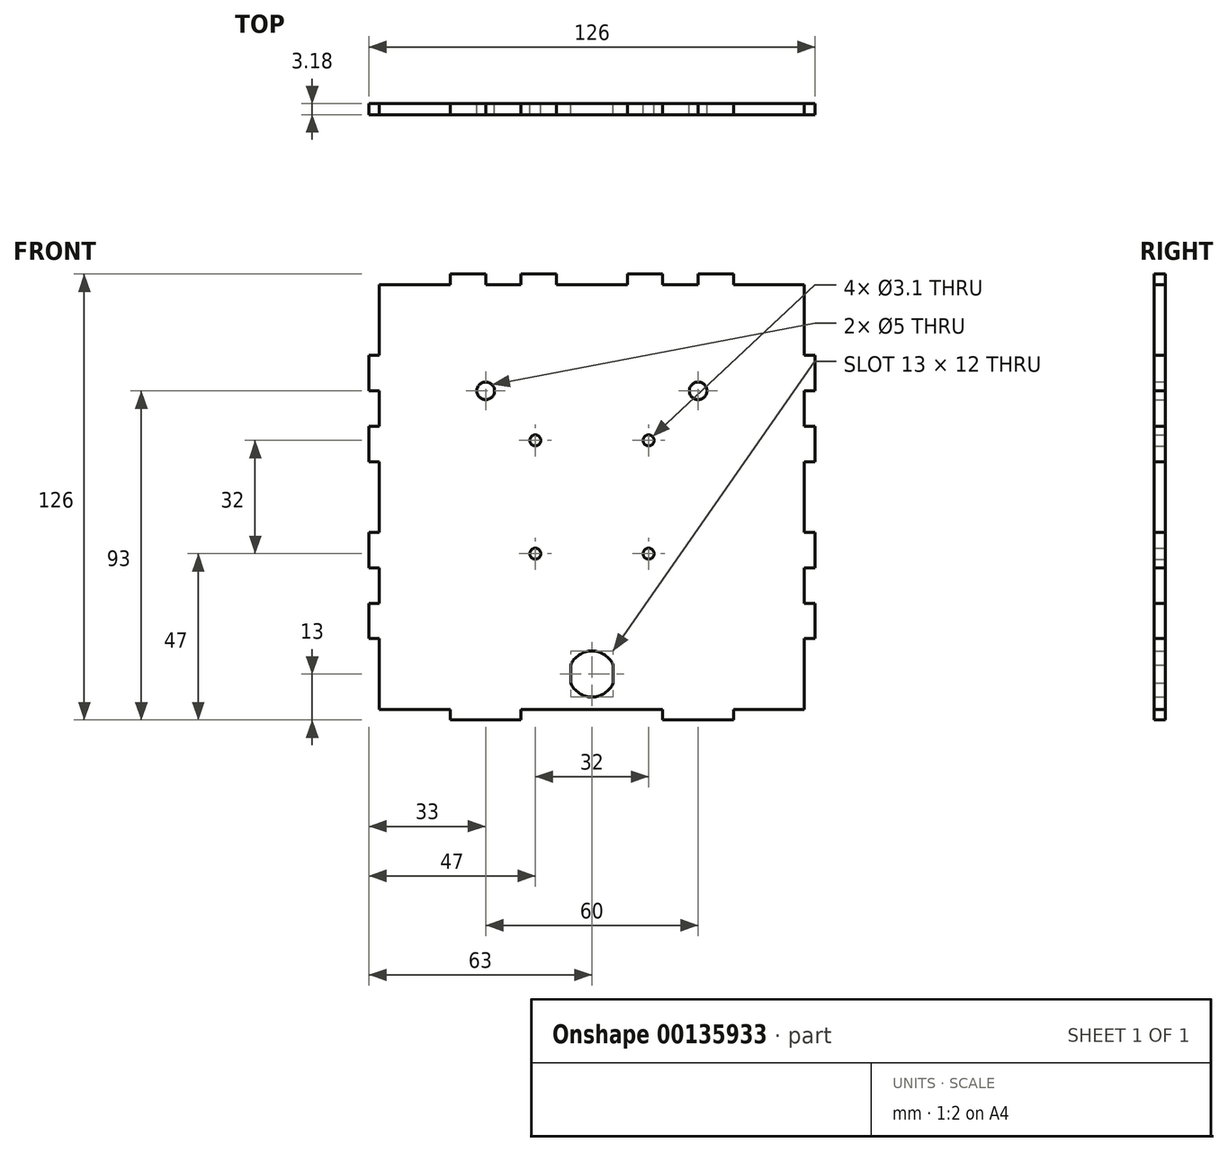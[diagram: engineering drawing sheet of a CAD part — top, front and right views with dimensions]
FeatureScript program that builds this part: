
annotation { "Feature Type Name" : "Feature", "Feature Type Description" : "" }
export const myFeature = defineFeature(function(context is Context, id is Id, definition is map)
    precondition{}
    {
        {
            var Q0;
            Q0=qCreatedBy(makeId("Front.planeOp"),FACE);
            var sketch = newSketch(context, id + "F0", { "sketchPlane" : qUnion([Q0])});
            skCircle(sketch, "E0", {"center": v(16, 16) * mm, "radius": 1.55 * mm});
            skCircle(sketch, "E1.1.0", {"center": v(-16, 16) * mm, "radius": 1.55 * mm});
            skCircle(sketch, "E1.2.0", {"center": v(-16, -16) * mm, "radius": 1.55 * mm});
            skCircle(sketch, "E1.3.0", {"center": v(16, -16) * mm, "radius": 1.55 * mm});
            skPoint(sketch, "E1.center", {"position": v(0, 0) * mm});
            skLineSegment(sketch, "E2", {"start": v(0, 60) * mm, "end": v(10, 60) * mm});
            skLineSegment(sketch, "E3", {"start": v(10, 60) * mm, "end": v(10, 63) * mm});
            skLineSegment(sketch, "E4", {"start": v(10, 63) * mm, "end": v(20, 63) * mm});
            skLineSegment(sketch, "E5", {"start": v(20, 63) * mm, "end": v(20, 60) * mm});
            skLineSegment(sketch, "E6", {"start": v(20, 60) * mm, "end": v(30, 60) * mm});
            skLineSegment(sketch, "E7", {"start": v(30, 60) * mm, "end": v(30, 63) * mm});
            skLineSegment(sketch, "E8", {"start": v(30, 63) * mm, "end": v(40, 63) * mm});
            skLineSegment(sketch, "E9", {"start": v(40, 63) * mm, "end": v(40, 60) * mm});
            skLineSegment(sketch, "E10", {"start": v(40, 60) * mm, "end": v(60, 60) * mm});
            skLineSegment(sketch, "E11", {"start": v(60, 60) * mm, "end": v(60, 40) * mm});
            skLineSegment(sketch, "E12", {"start": v(60, 40) * mm, "end": v(63, 40) * mm});
            skLineSegment(sketch, "E13", {"start": v(63, 40) * mm, "end": v(63, 30) * mm});
            skLineSegment(sketch, "E14", {"start": v(63, 30) * mm, "end": v(60, 30) * mm});
            skLineSegment(sketch, "E15", {"start": v(60, 30) * mm, "end": v(60, 20) * mm});
            skLineSegment(sketch, "E16", {"start": v(60, 20) * mm, "end": v(63, 20) * mm});
            skLineSegment(sketch, "E17", {"start": v(63, 20) * mm, "end": v(63, 10) * mm});
            skLineSegment(sketch, "E18", {"start": v(63, 10) * mm, "end": v(60, 10) * mm});
            skLineSegment(sketch, "E19", {"start": v(60, 10) * mm, "end": v(60, -10) * mm});
            skLineSegment(sketch, "E20", {"start": v(60, -10) * mm, "end": v(63, -10) * mm});
            skLineSegment(sketch, "E21", {"start": v(63, -10) * mm, "end": v(63, -20) * mm});
            skLineSegment(sketch, "E22", {"start": v(63, -20) * mm, "end": v(60, -20) * mm});
            skLineSegment(sketch, "E23", {"start": v(60, -20) * mm, "end": v(60, -30) * mm});
            skLineSegment(sketch, "E24", {"start": v(60, -30) * mm, "end": v(63, -30) * mm});
            skLineSegment(sketch, "E25", {"start": v(63, -30) * mm, "end": v(63, -40) * mm});
            skLineSegment(sketch, "E26", {"start": v(63, -40) * mm, "end": v(60, -40) * mm});
            skLineSegment(sketch, "E27", {"start": v(60, -40) * mm, "end": v(60, -60) * mm});
            skLineSegment(sketch, "E28", {"start": v(60, -60) * mm, "end": v(40, -60) * mm});
            skLineSegment(sketch, "E29", {"start": v(40, -60) * mm, "end": v(40, -63) * mm});
            skLineSegment(sketch, "E30", {"start": v(40, -63) * mm, "end": v(20, -63) * mm});
            skLineSegment(sketch, "E31", {"start": v(20, -63) * mm, "end": v(20, -60) * mm});
            skLineSegment(sketch, "E32", {"start": v(20, -60) * mm, "end": v(0, -60) * mm});
            skLineSegment(sketch, "E33.MirrorCS", {"start": v(-40, -60) * mm, "end": v(-40, -63) * mm});
            skLineSegment(sketch, "E34.MirrorCS", {"start": v(-20, -63) * mm, "end": v(-20, -60) * mm});
            skLineSegment(sketch, "E35.MirrorCS", {"start": v(-40, -63) * mm, "end": v(-20, -63) * mm});
            skLineSegment(sketch, "E36.MirrorCS", {"start": v(-20, -60) * mm, "end": v(0, -60) * mm});
            skLineSegment(sketch, "E37.MirrorCS", {"start": v(-60, 20) * mm, "end": v(-63, 20) * mm});
            skLineSegment(sketch, "E38.MirrorCS", {"start": v(-63, 10) * mm, "end": v(-60, 10) * mm});
            skLineSegment(sketch, "E39.MirrorCS", {"start": v(-63, -40) * mm, "end": v(-60, -40) * mm});
            skLineSegment(sketch, "E40.MirrorCS", {"start": v(-60, -10) * mm, "end": v(-63, -10) * mm});
            skLineSegment(sketch, "E41.MirrorCS", {"start": v(-60, -30) * mm, "end": v(-63, -30) * mm});
            skLineSegment(sketch, "E42.MirrorCS", {"start": v(-63, -20) * mm, "end": v(-60, -20) * mm});
            skLineSegment(sketch, "E43.MirrorCS", {"start": v(-60, -40) * mm, "end": v(-60, -60) * mm});
            skLineSegment(sketch, "E44.MirrorCS", {"start": v(-63, -10) * mm, "end": v(-63, -20) * mm});
            skLineSegment(sketch, "E45.MirrorCS", {"start": v(-63, -30) * mm, "end": v(-63, -40) * mm});
            skLineSegment(sketch, "E46.MirrorCS", {"start": v(-60, -20) * mm, "end": v(-60, -30) * mm});
            skLineSegment(sketch, "E47.MirrorCS", {"start": v(-60, 10) * mm, "end": v(-60, -10) * mm});
            skLineSegment(sketch, "E48.MirrorCS", {"start": v(-60, -60) * mm, "end": v(-40, -60) * mm});
            skLineSegment(sketch, "E49.MirrorCS", {"start": v(-63, 20) * mm, "end": v(-63, 10) * mm});
            skLineSegment(sketch, "E50.MirrorCS", {"start": v(-60, 30) * mm, "end": v(-60, 20) * mm});
            skLineSegment(sketch, "E51.MirrorCS", {"start": v(-63, 30) * mm, "end": v(-60, 30) * mm});
            skLineSegment(sketch, "E52.MirrorCS", {"start": v(-40, 63) * mm, "end": v(-40, 60) * mm});
            skLineSegment(sketch, "E53.MirrorCS", {"start": v(-10, 60) * mm, "end": v(-10, 63) * mm});
            skLineSegment(sketch, "E54.MirrorCS", {"start": v(-20, 63) * mm, "end": v(-20, 60) * mm});
            skLineSegment(sketch, "E55.MirrorCS", {"start": v(-30, 60) * mm, "end": v(-30, 63) * mm});
            skLineSegment(sketch, "E56.MirrorCS", {"start": v(-60, 40) * mm, "end": v(-63, 40) * mm});
            skLineSegment(sketch, "E57.MirrorCS", {"start": v(-40, 60) * mm, "end": v(-60, 60) * mm});
            skLineSegment(sketch, "E58.MirrorCS", {"start": v(0, 60) * mm, "end": v(-10, 60) * mm});
            skLineSegment(sketch, "E59.MirrorCS", {"start": v(-30, 63) * mm, "end": v(-40, 63) * mm});
            skLineSegment(sketch, "E60.MirrorCS", {"start": v(-10, 63) * mm, "end": v(-20, 63) * mm});
            skLineSegment(sketch, "E61.MirrorCS", {"start": v(-60, 60) * mm, "end": v(-60, 40) * mm});
            skLineSegment(sketch, "E62.MirrorCS", {"start": v(-63, 40) * mm, "end": v(-63, 30) * mm});
            skLineSegment(sketch, "E63.MirrorCS", {"start": v(-20, 60) * mm, "end": v(-30, 60) * mm});
            skCircle(sketch, "E64", {"center": v(30, 30) * mm, "radius": 2.5 * mm});
            skCircle(sketch, "E65.MirrorC", {"center": v(-30, 30) * mm, "radius": 2.5 * mm});
            skPoint(sketch, "E66.middle", {"position": v(0, -50) * mm});
            skPoint(sketch, "E67", {"position": v(-6, -47.5) * mm});
            skPoint(sketch, "E68", {"position": v(-6, -52.5) * mm});
            skPoint(sketch, "E69", {"position": v(6, -52.5) * mm});
            skPoint(sketch, "E70", {"position": v(6, -47.5) * mm});
            skArc(sketch, "E71", {"start": v(-6, -47.5) * mm, "mid": v(0, -43.5) * mm, "end": v(6, -47.5) * mm});
            skArc(sketch, "E72", {"start": v(-6, -52.5) * mm, "mid": v(0, -56.5) * mm, "end": v(6, -52.5) * mm});
            skLineSegment(sketch, "E73", {"start": v(-6, -47.5) * mm, "end": v(-6, -52.5) * mm});
            skLineSegment(sketch, "E74", {"start": v(6, -47.5) * mm, "end": v(6, -52.5) * mm});
            skSolve(sketch);
        }
        {
            var Q0;
            Q0=makeQuery(id+"F0.imprint","IMPRINT",FACE,{"disambiguationData":[TD([[makeQuery(id+"F0.imprint","IMPRINT",EDGE,{"derivedFrom":sQuery(id+"F0.wireOp",EDGE,"E0")}),-1.0]])]});
            extrude(context, id + "F1", {"entities" : qUnion([Q0]), "depth" : 3.17 * mm, "symmetric" : true});
        }
    });
